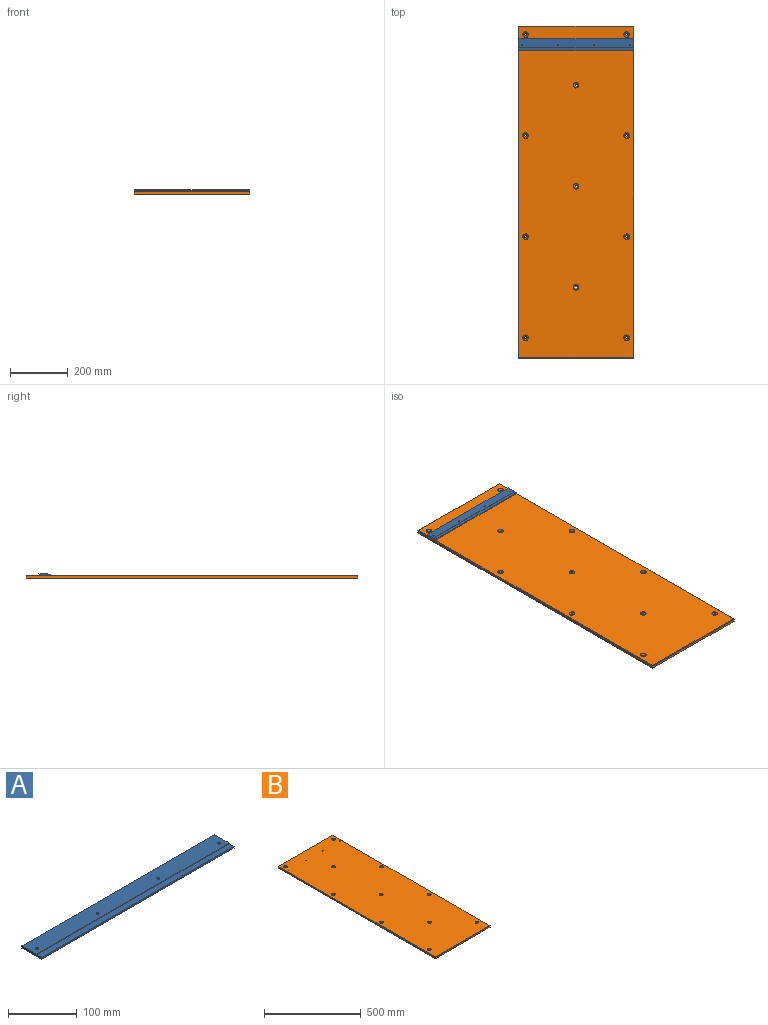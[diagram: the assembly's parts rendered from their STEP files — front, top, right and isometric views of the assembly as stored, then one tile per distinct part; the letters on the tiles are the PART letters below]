
ASSEMBLY  parts=2 mates=1
PART A: 12 faces, bbox 396x40x4 mm
  f0: plane 396x3mm, normal (0,-1,0), area 1188mm2, adj f1,f2,f5,f11
  f1: plane 40x4mm, normal (1,0,0), area 150mm2, adj f0,f3,f4,f5,f10,f11
  f2: plane 40x4mm, normal (-1,0,0), area 150mm2, adj f0,f3,f4,f5,f10,f11
  f3: plane 396x30mm, normal (0,0,1), area 11816.4mm2, adj f1,f2,f4,f6,f7,f8,f9,f10
  f4: plane 396x4mm, normal (0,1,0), area 1584mm2, adj f1,f2,f3,f5
  f5: plane 396x40mm, normal (0,0,-1), area 15776.4mm2, adj f0,f1,f2,f4,f6,f7,f8,f9
  f6: cylinder r=2.25mm len=4.5mm, axis (0,0,1), area 56.5mm2, adj f3,f5
  f7: cylinder r=2.25mm len=4.5mm, axis (0,0,1), area 56.5mm2, adj f3,f5
  f8: cylinder r=2.25mm len=4.5mm, axis (0,0,1), area 56.5mm2, adj f3,f5
  f9: cylinder r=2.25mm len=4.5mm, axis (0,0,1), area 56.5mm2, adj f3,f5
  f10: plane 396x1mm, normal (0,-1,0), area 396mm2, adj f1,f2,f3,f11
  f11: plane 396x10mm, normal (0,0,1), area 3960mm2, adj f0,f1,f2,f10
PART B: 47 faces, bbox 400x1150x10 mm
  f0: plane 400x8mm, normal (0,-1,0), area 3200mm2, adj f1,f3,f5,f40
  f1: plane 1150x8mm, normal (1,0,0), area 9200mm2, adj f0,f2,f5,f39
  f2: plane 400x8mm, normal (0,1,0), area 3200mm2, adj f1,f3,f5,f41
  f3: plane 1150x8mm, normal (-1,0,0), area 9200mm2, adj f0,f2,f5,f42
  f4: plane 1146x396mm, normal (0,0,1), area 450470.7mm2, adj f28,f29,f30,f31,f32,f33,f34,f35
  f5: plane 1150x400mm, normal (0,0,-1), area 459341.6mm2, adj f0,f1,f2,f3,f6,f8,f10,f12
  f6: cylinder r=4.25mm len=8.5mm, axis (0,0,1), area 141.3mm2, adj f5,f7
  f7: cone r=4.25mm half-angle=45deg, axis (0,0,1), area 231.3mm2, adj f6,f38
  f8: cylinder r=4.25mm len=8.5mm, axis (0,0,1), area 141.3mm2, adj f5,f9
  f9: cone r=4.25mm half-angle=45deg, axis (0,0,1), area 231.3mm2, adj f8,f37
  f10: cylinder r=4.25mm len=8.5mm, axis (0,0,1), area 141.3mm2, adj f5,f11
  f11: cone r=4.25mm half-angle=45deg, axis (0,0,1), area 231.3mm2, adj f10,f36
  f12: cylinder r=4.25mm len=8.5mm, axis (0,0,1), area 141.3mm2, adj f5,f13
  f13: cone r=4.25mm half-angle=45deg, axis (0,0,1), area 231.3mm2, adj f12,f35
  f14: cylinder r=4.25mm len=8.5mm, axis (0,0,1), area 141.3mm2, adj f5,f15
  f15: cone r=4.25mm half-angle=45deg, axis (0,0,1), area 231.3mm2, adj f14,f34
  f16: cylinder r=4.25mm len=8.5mm, axis (0,0,1), area 141.3mm2, adj f5,f17
  f17: cone r=4.25mm half-angle=45deg, axis (0,0,1), area 231.3mm2, adj f16,f33
  f18: cylinder r=4.25mm len=8.5mm, axis (0,0,1), area 141.3mm2, adj f5,f19
  f19: cone r=4.25mm half-angle=45deg, axis (0,0,1), area 231.3mm2, adj f18,f32
  f20: cylinder r=4.25mm len=8.5mm, axis (0,0,1), area 141.3mm2, adj f5,f21
  f21: cone r=4.25mm half-angle=45deg, axis (0,0,1), area 231.3mm2, adj f20,f31
  f22: cylinder r=4.25mm len=8.5mm, axis (0,0,1), area 141.3mm2, adj f5,f23
  f23: cone r=4.25mm half-angle=45deg, axis (0,0,1), area 231.3mm2, adj f22,f30
  f24: cylinder r=4.25mm len=8.5mm, axis (0,0,1), area 141.3mm2, adj f5,f25
  f25: cone r=4.25mm half-angle=45deg, axis (0,0,1), area 231.3mm2, adj f24,f29
  f26: cylinder r=4.25mm len=8.5mm, axis (0,0,1), area 141.3mm2, adj f5,f27
  f27: cone r=4.25mm half-angle=45deg, axis (0,0,1), area 231.3mm2, adj f26,f28
  f28: cone r=8.37mm half-angle=67.5deg, axis (0,0,1), area 87.3mm2, adj f4,f27
  f29: cone r=8.37mm half-angle=67.5deg, axis (0,0,1), area 87.3mm2, adj f4,f25
  f30: cone r=8.37mm half-angle=67.5deg, axis (0,0,1), area 87.3mm2, adj f4,f23
  f31: cone r=8.37mm half-angle=67.5deg, axis (0,0,1), area 87.3mm2, adj f4,f21
  f32: cone r=8.37mm half-angle=67.5deg, axis (0,0,1), area 87.3mm2, adj f4,f19
  f33: cone r=8.37mm half-angle=67.5deg, axis (0,0,1), area 87.3mm2, adj f4,f17
  f34: cone r=8.37mm half-angle=67.5deg, axis (0,0,1), area 87.3mm2, adj f4,f15
  f35: cone r=8.37mm half-angle=67.5deg, axis (0,0,1), area 87.3mm2, adj f4,f13
  f36: cone r=8.37mm half-angle=67.5deg, axis (0,0,1), area 87.3mm2, adj f4,f11
  f37: cone r=8.37mm half-angle=67.5deg, axis (0,0,1), area 87.3mm2, adj f4,f9
  f38: cone r=8.37mm half-angle=67.5deg, axis (0,0,1), area 87.3mm2, adj f4,f7
  f39: plane 1150x2mm, normal (0.71,0,0.71), area 3247mm2, adj f1,f4,f40,f41
  f40: plane 400x2mm, normal (0,-0.71,0.71), area 1125.7mm2, adj f0,f4,f39,f42
  f41: plane 400x2mm, normal (0,0.71,0.71), area 1125.7mm2, adj f2,f4,f39,f42
  f42: plane 1150x2mm, normal (-0.71,0,0.71), area 3247mm2, adj f3,f4,f40,f41
  f43: cylinder r=1.65mm len=10mm, axis (0,0,1), area 103.7mm2, adj f4,f5
  f44: cylinder r=1.65mm len=10mm, axis (0,0,1), area 103.7mm2, adj f4,f5
  f45: cylinder r=1.65mm len=10mm, axis (0,0,1), area 103.7mm2, adj f4,f5
  f46: cylinder r=1.65mm len=10mm, axis (0,0,1), area 103.7mm2, adj f4,f5
PLACE A t=(2.54,514.38,4.18)mm
PLACE B t=(2.54,4.38,-5.82)mm
MATE fastened A.f6 <-> B.f43  axis (0,0,-1) through (-184.96,514.38,4.18)mm
